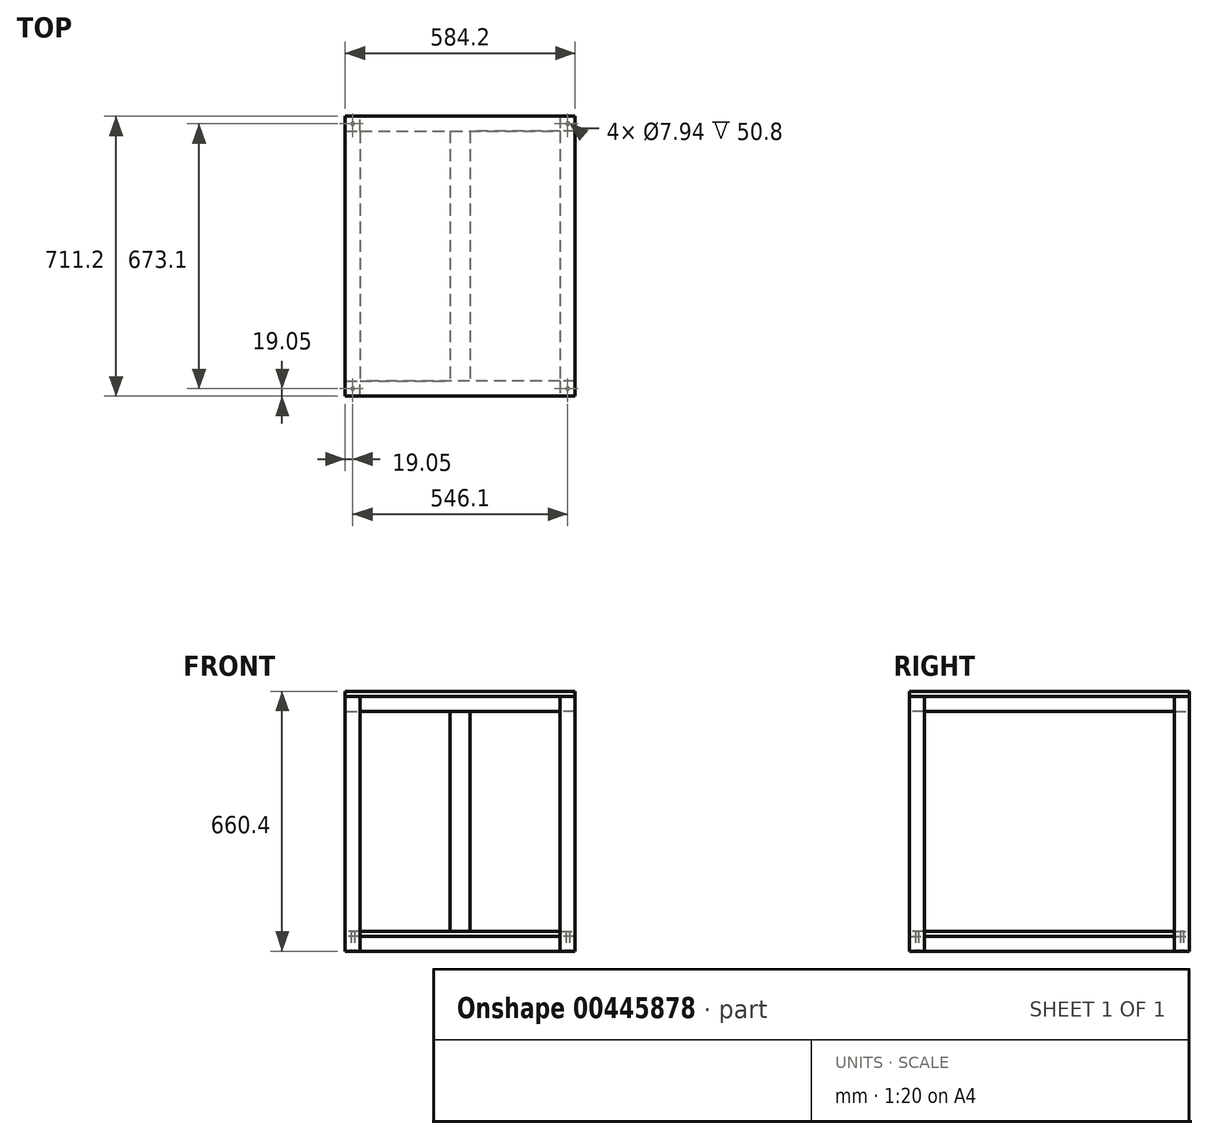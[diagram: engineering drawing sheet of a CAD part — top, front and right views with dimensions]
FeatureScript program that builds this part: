
annotation { "Feature Type Name" : "Feature", "Feature Type Description" : "" }
export const myFeature = defineFeature(function(context is Context, id is Id, definition is map)
    precondition{}
    {
        {
            var Q0;
            Q0=qCreatedBy(makeId("Top.planeOp"),FACE);
            var sketch = newSketch(context, id + "F0", { "sketchPlane" : qUnion([Q0])});
            skLineSegment(sketch, "E0", {"start": v(0, 317.5) * mm, "end": v(0, -317.5) * mm, "construction": true});
            skLineSegment(sketch, "E1.bottom", {"start": v(254, 317.5) * mm, "end": v(25.4, 317.5) * mm});
            skLineSegment(sketch, "E1.top", {"start": v(254, -317.5) * mm, "end": v(25.4, -317.5) * mm});
            skLineSegment(sketch, "E1.left", {"start": v(254, 317.5) * mm, "end": v(254, -317.5) * mm});
            skLineSegment(sketch, "E1.right", {"start": v(25.4, 317.5) * mm, "end": v(25.4, -317.5) * mm});
            skPoint(sketch, "E1.middle", {"position": v(139.7, 0) * mm});
            skLineSegment(sketch, "E2.MirrorCS", {"start": v(-254, 317.5) * mm, "end": v(-25.4, 317.5) * mm});
            skLineSegment(sketch, "E3.MirrorCS", {"start": v(-25.4, 317.5) * mm, "end": v(-25.4, -317.5) * mm});
            skLineSegment(sketch, "E4.MirrorCS", {"start": v(-254, 317.5) * mm, "end": v(-254, -317.5) * mm});
            skLineSegment(sketch, "E5.MirrorCS", {"start": v(-254, -317.5) * mm, "end": v(-25.4, -317.5) * mm});
            skSolve(sketch);
        }
        {
            var Q0;
            Q0 = qSketchRegion(id + "F0", true);
            extrude(context, id + "F1", {"entities" : qUnion([Q0]), "depth" : 558.8 * mm});
        }
        {
            var Q0;
            Q0=qCreatedBy(makeId("Top.planeOp"),FACE);
            var sketch = newSketch(context, id + "F2", { "sketchPlane" : qUnion([Q0])});
            skLineSegment(sketch, "E6.bottom", {"start": v(292.1, 355.6) * mm, "end": v(-292.1, 355.6) * mm, "construction": true});
            skLineSegment(sketch, "E6.top", {"start": v(292.1, -355.6) * mm, "end": v(-292.1, -355.6) * mm, "construction": true});
            skLineSegment(sketch, "E6.left", {"start": v(292.1, 355.6) * mm, "end": v(292.1, -355.6) * mm, "construction": true});
            skLineSegment(sketch, "E6.right", {"start": v(-292.1, 355.6) * mm, "end": v(-292.1, -355.6) * mm, "construction": true});
            skPoint(sketch, "E6.middle", {"position": v(0, 0) * mm});
            skLineSegment(sketch, "E7.bottom", {"start": v(-292.1, 355.6) * mm, "end": v(-254, 355.6) * mm});
            skLineSegment(sketch, "E7.top", {"start": v(-292.1, 317.5) * mm, "end": v(-254, 317.5) * mm});
            skLineSegment(sketch, "E7.left", {"start": v(-292.1, 355.6) * mm, "end": v(-292.1, 317.5) * mm});
            skLineSegment(sketch, "E7.right", {"start": v(-254, 355.6) * mm, "end": v(-254, 317.5) * mm});
            skLineSegment(sketch, "E8.bottom", {"start": v(292.1, 355.6) * mm, "end": v(254, 355.6) * mm});
            skLineSegment(sketch, "E8.top", {"start": v(292.1, 317.5) * mm, "end": v(254, 317.5) * mm});
            skLineSegment(sketch, "E8.left", {"start": v(292.1, 355.6) * mm, "end": v(292.1, 317.5) * mm});
            skLineSegment(sketch, "E8.right", {"start": v(254, 355.6) * mm, "end": v(254, 317.5) * mm});
            skLineSegment(sketch, "E9.bottom", {"start": v(292.1, -355.6) * mm, "end": v(254, -355.6) * mm});
            skLineSegment(sketch, "E9.top", {"start": v(292.1, -317.5) * mm, "end": v(254, -317.5) * mm});
            skLineSegment(sketch, "E9.left", {"start": v(292.1, -355.6) * mm, "end": v(292.1, -317.5) * mm});
            skLineSegment(sketch, "E9.right", {"start": v(254, -355.6) * mm, "end": v(254, -317.5) * mm});
            skLineSegment(sketch, "E10.bottom", {"start": v(-292.1, -355.6) * mm, "end": v(-254, -355.6) * mm});
            skLineSegment(sketch, "E10.top", {"start": v(-292.1, -317.5) * mm, "end": v(-254, -317.5) * mm});
            skLineSegment(sketch, "E10.left", {"start": v(-292.1, -355.6) * mm, "end": v(-292.1, -317.5) * mm});
            skLineSegment(sketch, "E10.right", {"start": v(-254, -355.6) * mm, "end": v(-254, -317.5) * mm});
            skSolve(sketch);
        }
        {
            var Q0;
            Q0 = qSketchRegion(id + "F2", true);
            extrude(context, id + "F3", {"entities" : qUnion([Q0]), "depth" : 596.9 * mm});
        }
        {
            var Q0;
            Q0=makeQuery(id+"F3.opExtrude","CAP_FACE",FACE,{"disambiguationData":[OSD([sQuery(id+"F2.wireOp",EDGE,"E10.bottom"),sQuery(id+"F2.wireOp",EDGE,"E10.top"),sQuery(id+"F2.wireOp",EDGE,"E10.left"),sQuery(id+"F2.wireOp",EDGE,"E10.right")])],"isStart":true});
            extrude(context, id + "F4", {"entities" : qUnion([Q0]), "operationType" : NewBodyOperationType.ADD, "depth" : 50.8 * mm});
        }
        {
            var Q0;
            Q0=makeQuery(id+"F3.opExtrude","CAP_FACE",FACE,{"disambiguationData":[OSD([sQuery(id+"F2.wireOp",EDGE,"E9.bottom"),sQuery(id+"F2.wireOp",EDGE,"E9.top"),sQuery(id+"F2.wireOp",EDGE,"E9.left"),sQuery(id+"F2.wireOp",EDGE,"E9.right")])],"isStart":true});
            extrude(context, id + "F5", {"entities" : qUnion([Q0]), "operationType" : NewBodyOperationType.ADD, "depth" : 50.8 * mm});
        }
        {
            var Q0;
            Q0=makeQuery(id+"F3.opExtrude","CAP_FACE",FACE,{"disambiguationData":[OSD([sQuery(id+"F2.wireOp",EDGE,"E7.bottom"),sQuery(id+"F2.wireOp",EDGE,"E7.top"),sQuery(id+"F2.wireOp",EDGE,"E7.left"),sQuery(id+"F2.wireOp",EDGE,"E7.right")])],"isStart":true});
            extrude(context, id + "F6", {"entities" : qUnion([Q0]), "operationType" : NewBodyOperationType.ADD, "depth" : 50.8 * mm});
        }
        {
            var Q0;
            Q0=makeQuery(id+"F3.opExtrude","CAP_FACE",FACE,{"disambiguationData":[OSD([sQuery(id+"F2.wireOp",EDGE,"E8.bottom"),sQuery(id+"F2.wireOp",EDGE,"E8.top"),sQuery(id+"F2.wireOp",EDGE,"E8.left"),sQuery(id+"F2.wireOp",EDGE,"E8.right")])],"isStart":true});
            extrude(context, id + "F7", {"entities" : qUnion([Q0]), "operationType" : NewBodyOperationType.ADD, "depth" : 50.8 * mm});
        }
        {
            var Q0;
            Q0=qCreatedBy(makeId("Top.planeOp"),FACE);
            var sketch = newSketch(context, id + "F8", { "sketchPlane" : qUnion([Q0])});
            skPoint(sketch, "E11.0", {"position": v(-254, 355.6) * mm});
            skPoint(sketch, "E12.0", {"position": v(-292.1, 317.5) * mm});
            skPoint(sketch, "E13.0", {"position": v(-254, 317.5) * mm});
            skPoint(sketch, "E14.0", {"position": v(254, 355.6) * mm});
            skPoint(sketch, "E15.0", {"position": v(254, 317.5) * mm});
            skPoint(sketch, "E16.0", {"position": v(292.1, 317.5) * mm});
            skPoint(sketch, "E17.0", {"position": v(254, -317.5) * mm});
            skPoint(sketch, "E18.0", {"position": v(292.1, -317.5) * mm});
            skPoint(sketch, "E19.0", {"position": v(254, -355.6) * mm});
            skPoint(sketch, "E20.0", {"position": v(-254, -355.6) * mm});
            skPoint(sketch, "E21.0", {"position": v(-254, -317.5) * mm});
            skPoint(sketch, "E22.0", {"position": v(-292.1, -317.5) * mm});
            skLineSegment(sketch, "E23", {"start": v(-292.1, 317.5) * mm, "end": v(-292.1, -317.5) * mm});
            skLineSegment(sketch, "E24", {"start": v(-292.1, -317.5) * mm, "end": v(-254, -317.5) * mm});
            skLineSegment(sketch, "E25", {"start": v(-254, -317.5) * mm, "end": v(-254, -355.6) * mm});
            skLineSegment(sketch, "E26", {"start": v(254, -355.6) * mm, "end": v(-254, -355.6) * mm});
            skLineSegment(sketch, "E27", {"start": v(254, -317.5) * mm, "end": v(254, -355.6) * mm});
            skLineSegment(sketch, "E28", {"start": v(254, -317.5) * mm, "end": v(292.1, -317.5) * mm});
            skLineSegment(sketch, "E29", {"start": v(292.1, -317.5) * mm, "end": v(292.1, 317.5) * mm});
            skLineSegment(sketch, "E30", {"start": v(292.1, 317.5) * mm, "end": v(254, 317.5) * mm});
            skLineSegment(sketch, "E31", {"start": v(254, 317.5) * mm, "end": v(254, 355.6) * mm});
            skLineSegment(sketch, "E32", {"start": v(254, 355.6) * mm, "end": v(-254, 355.6) * mm});
            skLineSegment(sketch, "E33", {"start": v(-254, 355.6) * mm, "end": v(-254, 317.5) * mm});
            skLineSegment(sketch, "E34", {"start": v(-254, 317.5) * mm, "end": v(-292.1, 317.5) * mm});
            skSolve(sketch);
        }
        {
            var Q0;
            Q0 = qSketchRegion(id + "F8", true);
            extrude(context, id + "F9", {"entities" : qUnion([Q0]), "oppositeDirection" : true, "depth" : 12.7 * mm});
        }
        {
            var Q0;
            Q0=makeQuery(id+"F6.opExtrude","CAP_FACE",FACE,{"disambiguationData":[OSD([sQuery(id+"F2.wireOp",EDGE,"E7.bottom"),sQuery(id+"F2.wireOp",EDGE,"E7.top"),sQuery(id+"F2.wireOp",EDGE,"E7.left"),sQuery(id+"F2.wireOp",EDGE,"E7.right")])],"isStart":false});
            var sketch = newSketch(context, id + "F10", { "sketchPlane" : qUnion([Q0])});
            skPoint(sketch, "E35.0", {"position": v(254, 355.6) * mm});
            skPoint(sketch, "E36.0", {"position": v(-254, 317.5) * mm});
            skPoint(sketch, "E37.0", {"position": v(-292.1, -317.5) * mm});
            skPoint(sketch, "E38.0", {"position": v(-254, -317.5) * mm});
            skPoint(sketch, "E39.0", {"position": v(254, -355.6) * mm});
            skPoint(sketch, "E40.0", {"position": v(292.1, -317.5) * mm});
            skPoint(sketch, "E41.0", {"position": v(254, 317.5) * mm});
            skLineSegment(sketch, "E42.bottom", {"start": v(254, 355.6) * mm, "end": v(-254, 355.6) * mm});
            skLineSegment(sketch, "E42.top", {"start": v(254, 317.5) * mm, "end": v(-254, 317.5) * mm});
            skLineSegment(sketch, "E42.left", {"start": v(254, 355.6) * mm, "end": v(254, 317.5) * mm});
            skLineSegment(sketch, "E42.right", {"start": v(-254, 355.6) * mm, "end": v(-254, 317.5) * mm});
            skLineSegment(sketch, "E43.bottom", {"start": v(-254, 317.5) * mm, "end": v(-292.1, 317.5) * mm});
            skLineSegment(sketch, "E43.top", {"start": v(-254, -317.5) * mm, "end": v(-292.1, -317.5) * mm});
            skLineSegment(sketch, "E43.left", {"start": v(-254, 317.5) * mm, "end": v(-254, -317.5) * mm});
            skLineSegment(sketch, "E43.right", {"start": v(-292.1, 317.5) * mm, "end": v(-292.1, -317.5) * mm});
            skLineSegment(sketch, "E44.bottom", {"start": v(-254, -317.5) * mm, "end": v(254, -317.5) * mm});
            skLineSegment(sketch, "E44.top", {"start": v(-254, -355.6) * mm, "end": v(254, -355.6) * mm});
            skLineSegment(sketch, "E44.left", {"start": v(-254, -317.5) * mm, "end": v(-254, -355.6) * mm});
            skLineSegment(sketch, "E44.right", {"start": v(254, -317.5) * mm, "end": v(254, -355.6) * mm});
            skLineSegment(sketch, "E45.bottom", {"start": v(292.1, -317.5) * mm, "end": v(254, -317.5) * mm});
            skLineSegment(sketch, "E45.top", {"start": v(292.1, 317.5) * mm, "end": v(254, 317.5) * mm});
            skLineSegment(sketch, "E45.left", {"start": v(292.1, -317.5) * mm, "end": v(292.1, 317.5) * mm});
            skLineSegment(sketch, "E45.right", {"start": v(254, -317.5) * mm, "end": v(254, 317.5) * mm});
            skSolve(sketch);
        }
        {
            var Q0;
            Q0=makeQuery(id+"F10.imprint","IMPRINT",FACE,{"disambiguationData":[TD([[makeQuery(id+"F10.imprint","IMPRINT",EDGE,{"derivedFrom":sQuery(id+"F10.wireOp",EDGE,"E45.bottom")}),-1.0]])]});
            var Q1;
            Q1=makeQuery(id+"F10.imprint","IMPRINT",FACE,{"disambiguationData":[TD([[makeQuery(id+"F10.imprint","IMPRINT",EDGE,{"derivedFrom":sQuery(id+"F10.wireOp",EDGE,"E44.bottom")}),-1.0]])]});
            var Q2;
            Q2=makeQuery(id+"F10.imprint","IMPRINT",FACE,{"disambiguationData":[TD([[makeQuery(id+"F10.imprint","IMPRINT",EDGE,{"derivedFrom":sQuery(id+"F10.wireOp",EDGE,"E43.bottom")}),1.0]])]});
            var Q3;
            Q3=makeQuery(id+"F10.imprint","IMPRINT",FACE,{"disambiguationData":[TD([[makeQuery(id+"F10.imprint","IMPRINT",EDGE,{"derivedFrom":sQuery(id+"F10.wireOp",EDGE,"E42.bottom")}),1.0]])]});
            extrude(context, id + "F11", {"entities" : qUnion([Q0, Q1, Q2, Q3]), "oppositeDirection" : true, "depth" : 38.1 * mm});
        }
        {
            var Q0;
            Q0=makeQuery(id+"F3.opExtrude","CAP_FACE",FACE,{"disambiguationData":[OSD([sQuery(id+"F2.wireOp",EDGE,"E8.bottom"),sQuery(id+"F2.wireOp",EDGE,"E8.top"),sQuery(id+"F2.wireOp",EDGE,"E8.left"),sQuery(id+"F2.wireOp",EDGE,"E8.right")])],"isStart":false});
            var sketch = newSketch(context, id + "F12", { "sketchPlane" : qUnion([Q0])});
            skPoint(sketch, "E46.0", {"position": v(254, -317.5) * mm});
            skPoint(sketch, "E47.0", {"position": v(-254, -355.6) * mm});
            skPoint(sketch, "E48.0", {"position": v(-292.1, -317.5) * mm});
            skPoint(sketch, "E49.0", {"position": v(-254, 317.5) * mm});
            skPoint(sketch, "E50.0", {"position": v(254, 355.6) * mm});
            skPoint(sketch, "E51.0", {"position": v(292.1, 317.5) * mm});
            skLineSegment(sketch, "E52.bottom", {"start": v(254, -317.5) * mm, "end": v(-254, -317.5) * mm});
            skLineSegment(sketch, "E52.top", {"start": v(254, -355.6) * mm, "end": v(-254, -355.6) * mm});
            skLineSegment(sketch, "E52.left", {"start": v(254, -317.5) * mm, "end": v(254, -355.6) * mm});
            skLineSegment(sketch, "E52.right", {"start": v(-254, -317.5) * mm, "end": v(-254, -355.6) * mm});
            skLineSegment(sketch, "E53.bottom", {"start": v(-292.1, -317.5) * mm, "end": v(-254, -317.5) * mm});
            skLineSegment(sketch, "E53.top", {"start": v(-292.1, 317.5) * mm, "end": v(-254, 317.5) * mm});
            skLineSegment(sketch, "E53.left", {"start": v(-292.1, -317.5) * mm, "end": v(-292.1, 317.5) * mm});
            skLineSegment(sketch, "E53.right", {"start": v(-254, -317.5) * mm, "end": v(-254, 317.5) * mm});
            skLineSegment(sketch, "E54.bottom", {"start": v(-254, 317.5) * mm, "end": v(254, 317.5) * mm});
            skLineSegment(sketch, "E54.top", {"start": v(-254, 355.6) * mm, "end": v(254, 355.6) * mm});
            skLineSegment(sketch, "E54.left", {"start": v(-254, 317.5) * mm, "end": v(-254, 355.6) * mm});
            skLineSegment(sketch, "E54.right", {"start": v(254, 317.5) * mm, "end": v(254, 355.6) * mm});
            skLineSegment(sketch, "E55.bottom", {"start": v(292.1, 317.5) * mm, "end": v(254, 317.5) * mm});
            skLineSegment(sketch, "E55.top", {"start": v(292.1, -317.5) * mm, "end": v(254, -317.5) * mm});
            skLineSegment(sketch, "E55.left", {"start": v(292.1, 317.5) * mm, "end": v(292.1, -317.5) * mm});
            skLineSegment(sketch, "E55.right", {"start": v(254, 317.5) * mm, "end": v(254, -317.5) * mm});
            skSolve(sketch);
        }
        {
            var Q0;
            Q0=makeQuery(id+"F12.imprint","IMPRINT",FACE,{"disambiguationData":[TD([[makeQuery(id+"F12.imprint","IMPRINT",EDGE,{"derivedFrom":sQuery(id+"F12.wireOp",EDGE,"E52.bottom")}),1.0]])]});
            var Q1;
            Q1=makeQuery(id+"F12.imprint","IMPRINT",FACE,{"disambiguationData":[TD([[makeQuery(id+"F12.imprint","IMPRINT",EDGE,{"derivedFrom":sQuery(id+"F12.wireOp",EDGE,"E55.bottom")}),1.0]])]});
            var Q2;
            Q2=makeQuery(id+"F12.imprint","IMPRINT",FACE,{"disambiguationData":[TD([[makeQuery(id+"F12.imprint","IMPRINT",EDGE,{"derivedFrom":sQuery(id+"F12.wireOp",EDGE,"E54.bottom")}),1.0]])]});
            var Q3;
            Q3=makeQuery(id+"F12.imprint","IMPRINT",FACE,{"disambiguationData":[TD([[makeQuery(id+"F12.imprint","IMPRINT",EDGE,{"derivedFrom":sQuery(id+"F12.wireOp",EDGE,"E53.bottom")}),1.0]])]});
            extrude(context, id + "F13", {"entities" : qUnion([Q0, Q1, Q2, Q3]), "oppositeDirection" : true, "depth" : 38.1 * mm});
        }
        {
            var Q0;
            Q0=makeQuery(id+"F3.opExtrude","CAP_FACE",FACE,{"disambiguationData":[OSD([sQuery(id+"F2.wireOp",EDGE,"E9.bottom"),sQuery(id+"F2.wireOp",EDGE,"E9.top"),sQuery(id+"F2.wireOp",EDGE,"E9.left"),sQuery(id+"F2.wireOp",EDGE,"E9.right")])],"isStart":false});
            var sketch = newSketch(context, id + "F14", { "sketchPlane" : qUnion([Q0])});
            skPoint(sketch, "E56.0", {"position": v(-292.1, 355.6) * mm});
            skPoint(sketch, "E57.0", {"position": v(292.1, -355.6) * mm});
            skLineSegment(sketch, "E58.bottom", {"start": v(292.1, -355.6) * mm, "end": v(-292.1, -355.6) * mm});
            skLineSegment(sketch, "E58.top", {"start": v(292.1, 355.6) * mm, "end": v(-292.1, 355.6) * mm});
            skLineSegment(sketch, "E58.left", {"start": v(292.1, -355.6) * mm, "end": v(292.1, 355.6) * mm});
            skLineSegment(sketch, "E58.right", {"start": v(-292.1, -355.6) * mm, "end": v(-292.1, 355.6) * mm});
            skSolve(sketch);
        }
        {
            var Q0;
            Q0 = qSketchRegion(id + "F14", true);
            extrude(context, id + "F15", {"entities" : qUnion([Q0]), "depth" : 12.7 * mm});
        }
        {
            var Q0;
            Q0=makeQuery(id+"F7.opExtrude","CAP_FACE",FACE,{"disambiguationData":[OSD([sQuery(id+"F2.wireOp",EDGE,"E8.bottom"),sQuery(id+"F2.wireOp",EDGE,"E8.top"),sQuery(id+"F2.wireOp",EDGE,"E8.left"),sQuery(id+"F2.wireOp",EDGE,"E8.right")])],"isStart":false});
            var sketch = newSketch(context, id + "F16", { "sketchPlane" : qUnion([Q0])});
            skLineSegment(sketch, "E59.0.0", {"start": v(292.1, -317.5) * mm, "end": v(254, -317.5) * mm, "construction": true});
            skLineSegment(sketch, "E59.0.1", {"start": v(254, -317.5) * mm, "end": v(254, -355.6) * mm, "construction": true});
            skLineSegment(sketch, "E59.0.2", {"start": v(254, -355.6) * mm, "end": v(292.1, -355.6) * mm, "construction": true});
            skLineSegment(sketch, "E59.0.3", {"start": v(292.1, -355.6) * mm, "end": v(292.1, -317.5) * mm, "construction": true});
            skLineSegment(sketch, "E60.0.0", {"start": v(-292.1, -317.5) * mm, "end": v(-292.1, -355.6) * mm, "construction": true});
            skLineSegment(sketch, "E60.0.1", {"start": v(-292.1, -355.6) * mm, "end": v(-254, -355.6) * mm, "construction": true});
            skLineSegment(sketch, "E60.0.2", {"start": v(-254, -355.6) * mm, "end": v(-254, -317.5) * mm, "construction": true});
            skLineSegment(sketch, "E60.0.3", {"start": v(-254, -317.5) * mm, "end": v(-292.1, -317.5) * mm, "construction": true});
            skLineSegment(sketch, "E61.0.0", {"start": v(292.1, 317.5) * mm, "end": v(292.1, 355.6) * mm, "construction": true});
            skLineSegment(sketch, "E61.0.1", {"start": v(292.1, 355.6) * mm, "end": v(254, 355.6) * mm, "construction": true});
            skLineSegment(sketch, "E61.0.2", {"start": v(254, 355.6) * mm, "end": v(254, 317.5) * mm, "construction": true});
            skLineSegment(sketch, "E61.0.3", {"start": v(254, 317.5) * mm, "end": v(292.1, 317.5) * mm, "construction": true});
            skLineSegment(sketch, "E62.0.0", {"start": v(-292.1, 317.5) * mm, "end": v(-254, 317.5) * mm, "construction": true});
            skLineSegment(sketch, "E62.0.1", {"start": v(-254, 317.5) * mm, "end": v(-254, 355.6) * mm, "construction": true});
            skLineSegment(sketch, "E62.0.2", {"start": v(-254, 355.6) * mm, "end": v(-292.1, 355.6) * mm, "construction": true});
            skLineSegment(sketch, "E62.0.3", {"start": v(-292.1, 355.6) * mm, "end": v(-292.1, 317.5) * mm, "construction": true});
            skCircle(sketch, "E63", {"center": v(273.05, -336.55) * mm, "radius": 3.97 * mm});
            skPoint(sketch, "E63.centerSnap0", {"position": v(254, -336.55) * mm});
            skPoint(sketch, "E63.centerSnap1", {"position": v(273.05, -355.6) * mm});
            skCircle(sketch, "E64", {"center": v(-273.05, -336.55) * mm, "radius": 3.97 * mm});
            skPoint(sketch, "E64.centerSnap0", {"position": v(-273.05, -355.6) * mm});
            skPoint(sketch, "E64.centerSnap1", {"position": v(-292.1, -336.55) * mm});
            skCircle(sketch, "E65", {"center": v(273.05, 336.55) * mm, "radius": 3.97 * mm});
            skPoint(sketch, "E65.centerSnap0", {"position": v(254, 336.55) * mm});
            skPoint(sketch, "E65.centerSnap1", {"position": v(273.05, 317.5) * mm});
            skCircle(sketch, "E66", {"center": v(-273.05, 336.55) * mm, "radius": 3.97 * mm});
            skPoint(sketch, "E66.centerSnap0", {"position": v(-292.1, 336.55) * mm});
            skPoint(sketch, "E66.centerSnap1", {"position": v(-273.05, 317.5) * mm});
            skSolve(sketch);
        }
        {
            var Q0;
            Q0 = qSketchRegion(id + "F16", true);
            extrude(context, id + "F17", {"entities" : qUnion([Q0]), "operationType" : NewBodyOperationType.REMOVE, "oppositeDirection" : true, "depth" : 50.8 * mm});
        }
    });
